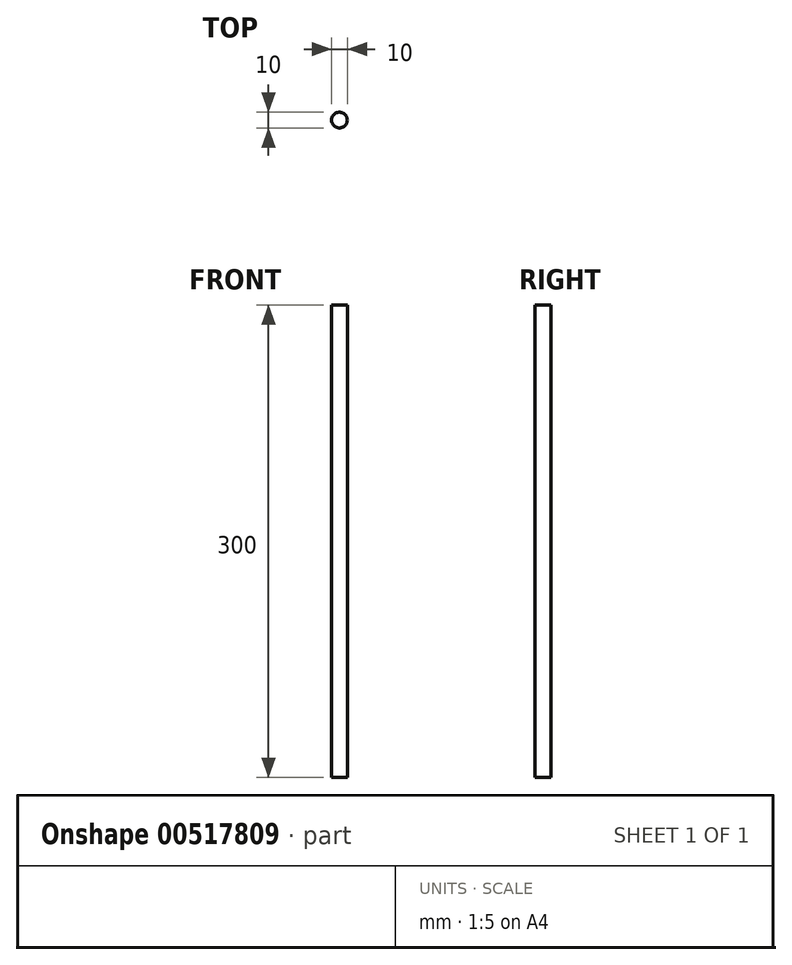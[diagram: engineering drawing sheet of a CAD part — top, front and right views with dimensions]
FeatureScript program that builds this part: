
annotation { "Feature Type Name" : "Feature", "Feature Type Description" : "" }
export const myFeature = defineFeature(function(context is Context, id is Id, definition is map)
    precondition{}
    {
        {
            var Q0;
            Q0=qCreatedBy(makeId("Top.planeOp"),FACE);
            var sketch = newSketch(context, id + "F0", { "sketchPlane" : qUnion([Q0])});
            skCircle(sketch, "E0", {"center": v(0, 0) * mm, "radius": 5 * mm});
            skSolve(sketch);
        }
        {
            var Q0;
            Q0 = qSketchRegion(id + "F0", true);
            extrude(context, id + "F1", {"entities" : qUnion([Q0]), "depth" : 300 * mm, "offsetDistance" : 25 * mm});
        }
    });
